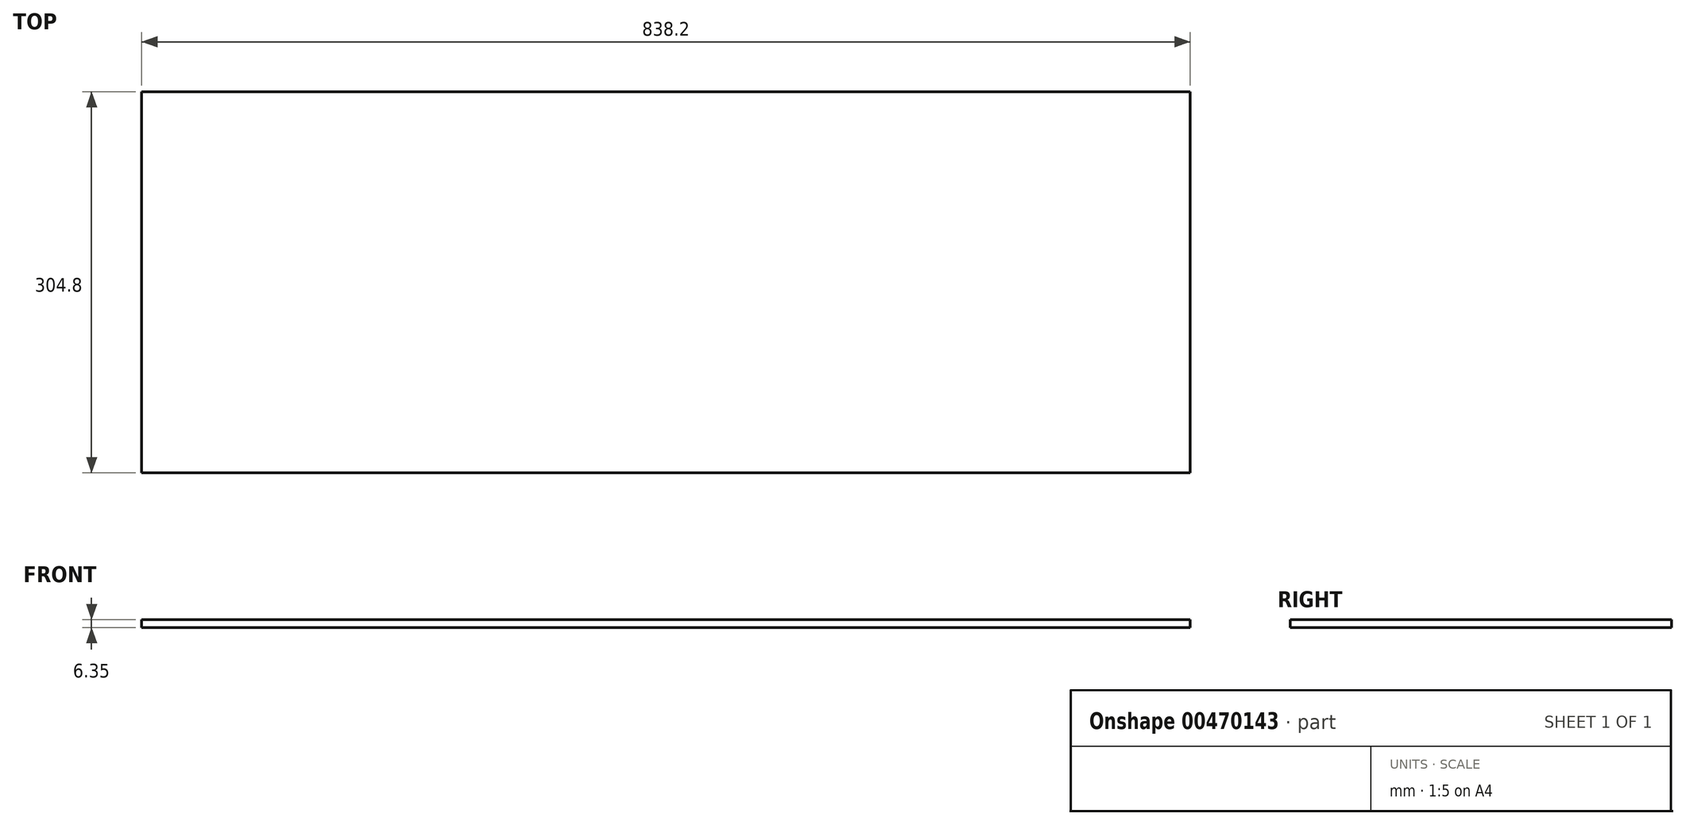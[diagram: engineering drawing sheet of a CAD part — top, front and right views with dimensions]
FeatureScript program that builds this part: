
annotation { "Feature Type Name" : "Feature", "Feature Type Description" : "" }
export const myFeature = defineFeature(function(context is Context, id is Id, definition is map)
    precondition{}
    {
        {
            var Q0;
            Q0=qCreatedBy(makeId("Top.planeOp"),FACE);
            var sketch = newSketch(context, id + "F0", { "sketchPlane" : qUnion([Q0])});
            skLineSegment(sketch, "E0.bottom", {"start": v(419.1, 152.4) * mm, "end": v(-419.1, 152.4) * mm});
            skLineSegment(sketch, "E0.top", {"start": v(419.1, -152.4) * mm, "end": v(-419.1, -152.4) * mm});
            skLineSegment(sketch, "E0.left", {"start": v(419.1, 152.4) * mm, "end": v(419.1, -152.4) * mm});
            skLineSegment(sketch, "E0.right", {"start": v(-419.1, 152.4) * mm, "end": v(-419.1, -152.4) * mm});
            skPoint(sketch, "E0.middle", {"position": v(0, 0) * mm});
            skSolve(sketch);
        }
        {
            var Q0;
            Q0=makeQuery(id+"F0.imprint","IMPRINT",FACE,{"disambiguationData":[TD([[makeQuery(id+"F0.imprint","IMPRINT",EDGE,{"derivedFrom":sQuery(id+"F0.wireOp",EDGE,"E0.bottom")}),1.0]])]});
            extrude(context, id + "F1", {"entities" : qUnion([Q0]), "depth" : 6.35 * mm});
        }
    });
